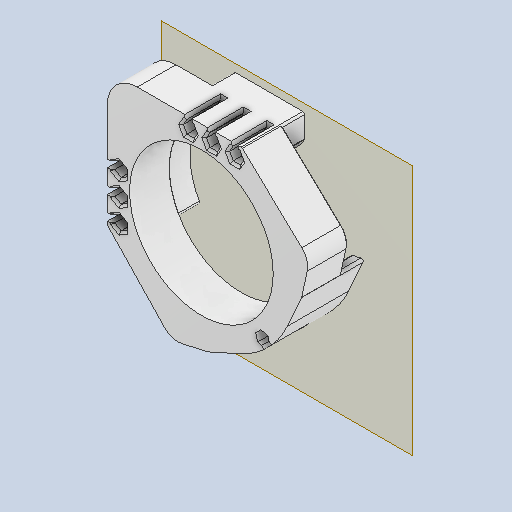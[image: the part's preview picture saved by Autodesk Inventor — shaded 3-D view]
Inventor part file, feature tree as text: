
AUTODESK INVENTOR PART (.ipt)
format: ipt  version: 2022 (Build 260153000, 153)  size: 1,166,336 bytes
history: native  units: in
note: dims shown in document units (in); Inventor stores cm internally (conversion verified against a paired STEP export)
features: reference x7, extrude x5, fillet x4, sketch x4, chamfer x4, other x4, projected_geometry x3, plane x2, pattern_circular x1
ambient origin geometry x8: Origin, YZ Plane, XZ Plane, XY Plane, X Axis, Y Axis, Z Axis, Center Point
bodies: Solid1 (feature_tree)
feature tree (34):
  plane  "Work Plane1"
  extrude  "Extrusion1"  Depth=0.0394in TaperAngle=0.0deg
  fillet  "Fillet1"  Radius=0.0394in
  sketch  "Sketch2"  dims[d10=0.4724in d11=0.0in d12=0.15in d13=0.0in]
  plane  "Work Plane2"
  extrude  "Extrusion2"  Depth=0.15in TaperAngle=0.0deg
  extrude  "Extrusion3"  Depth=1.5in
  chamfer  "Chamfer4"  Distance=2.0in
  fillet  "Fillet4"  Radius=3.1in
  fillet  "Fillet5"  Radius=1.1811in
  pattern_circular  "Circular Pattern1"  Angle=45.0deg  [1 undecoded]
  chamfer  "Chamfer2"  Distance=0.0236in Angle=45.0deg
  chamfer  "Chamfer3"  Distance=0.1106in Angle=45.0deg
  extrude  "Extrusion5"  Depth=0.0394in
  chamfer  "Chamfer5"  Distance=0.1969in
  fillet  "Fillet6"  Radius=0.0472in
  extrude  "Extrusion6"  Depth=0.2756in
  sketch  "Sketch1"  dims[d0=1.2598in d1=0.4724in d2=0.0in d3=0.0394in]
  reference  "Reference1"
  reference  "Reference2"
  reference  "Reference8"
  reference  "Reference9"
  reference  "Reference10"
  sketch  "Sketch3"  dims[d17=1.1811in d18=360.0deg d20=1.5in]
  reference  "Reference11"
  projected_geometry  "Projected Loop7"
  projected_geometry  "Projected Loop8"
  projected_geometry  "Projected Loop9"
  reference  "Reference12"
  sketch  "Sketch6"  dims[d21=1.5in d22=2.0in d23=3.1in d24=1.1811in d26=360.0deg d28=0.0236in d29=0.125in d30=45.0deg d31=0.0236in d32=0.125in d33=45.0deg d34=0.1106in d35=0.125in d36=45.0deg d48=0.0394in d49=0.1969in d50=0.0472in d51=0.2756in d52=0.7723in d53=0.0in d54=0.0472in d55=0.125in d56=45.0deg d59=45.0deg d60=0.0472in d61=1.0in d62=0.0in]
  other  "<userpath>\Documents\CAD\guardSwerve1\Assembly1.iam"
  other  "Assembly1.iam"
  other  "lower_plate:1"
  other  "uppermidblock:1"
note: 1 required parameter value undecoded (feature->parameter linkage not recoverable at this tier; creation-order binding heuristic only, values carry confidence <= 0.55)
